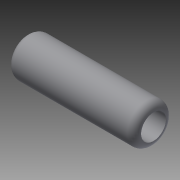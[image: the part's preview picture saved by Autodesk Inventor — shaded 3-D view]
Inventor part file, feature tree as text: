
AUTODESK INVENTOR PART (.ipt)
format: ipt  version: 2015 (Build 190159000, 159)  size: 106,496 bytes
history: native  units: in
note: dims shown in document units (in); Inventor stores cm internally (conversion verified against a paired STEP export)
features: fillet x2, revolve x1, sketch x1
ambient origin geometry x8: Origin, YZ Plane, XZ Plane, XY Plane, X Axis, Y Axis, Z Axis, Center Point
bodies: Solid1 (feature_tree)
feature tree (4):
  revolve  "Revolution1"  [1 undecoded]
  fillet  "Fillet1"  Radius=0.25in
  fillet  "Fillet2"  Radius=4.469in
  sketch  "Sketch1"  dims[d0=0.5938in d1=0.3438in d2=0.25in d3=4.469in d4=0.156in d5=4.469in d6=0.0938in d7=90.0deg d8=0.25in d9=0.25in]
note: 1 required parameter value undecoded (feature->parameter linkage not recoverable at this tier; creation-order binding heuristic only, values carry confidence <= 0.55)
